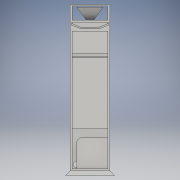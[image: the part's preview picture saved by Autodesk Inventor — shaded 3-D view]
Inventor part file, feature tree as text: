
AUTODESK INVENTOR PART (.ipt)
format: ipt  version: 2016 (Build 200138000, 138)  size: 480,768 bytes
history: native  units: in
note: dims shown in document units (in); Inventor stores cm internally (conversion verified against a paired STEP export)
features: sketch x19, extrude x18, chamfer x1, plane x1, loft x1, shell x1, fillet x1
ambient origin geometry x8: Origin, YZ Plane, XZ Plane, XY Plane, X Axis, Y Axis, Z Axis, Center Point
bodies: Solid1 (feature_tree)
feature tree (42):
  extrude  "Extrusion1"  Depth=18.0in
  extrude  "Extrusion3"  Depth=1.0in
  extrude  "Extrusion4"  Depth=1.0in
  extrude  "Extrusion7"  Depth=2.0in
  extrude  "Extrusion8"  Depth=16.2in
  chamfer  "Chamfer2"  Distance=13.3in
  extrude  "Extrusion9"  Depth=2.0in
  extrude  "Extrusion10"  Depth=2.0in TaperAngle=0.0deg
  sketch  "Sketch12"  dims[d13=2.0in]
  plane  "Work Plane1"
  loft  "Loft1"
  shell  "Shell1"  Thickness=17.0in
  extrude  "Extrusion12"  Depth=2.5in
  extrude  "Extrusion13"  Depth=2.5in
  extrude  "Extrusion14"  Depth=2.5in
  extrude  "Extrusion15"  TaperAngle=0.0deg  [1 undecoded]
  extrude  "Extrusion16"  TaperAngle=0.0deg  [1 undecoded]
  extrude  "Extrusion17"  Depth=2.5in
  extrude  "Extrusion18"  Depth=2.5in TaperAngle=0.0deg
  extrude  "Extrusion19"  Depth=2.5in
  extrude  "Extrusion20"  Depth=2.5in TaperAngle=0.0deg
  extrude  "Extrusion21"  Depth=2.5in
  extrude  "Extrusion22"  Depth=2.5in TaperAngle=0.0deg
  fillet  "Fillet1"  Radius=10.0in
  sketch  "Sketch1"  dims[d0=64.0in d1=18.0in]
  sketch  "Sketch3"  dims[d2=4.0in d3=1.0in]
  sketch  "Sketch4"  dims[d4=1.0in d5=1.0in]
  sketch  "Sketch7"  dims[d6=1.0in d7=2.0in]
  sketch  "Sketch8"  dims[d9=2.0in d10=16.2in]
  sketch  "Sketch9"  dims[d11=8.1in]
  sketch  "Sketch10"  dims[d12=2.56in]
  sketch  "Sketch13"  dims[d14=5.0in]
  sketch  "Sketch14"  dims[d15=5.0in]
  sketch  "Sketch15"  dims[d16=2.0in]
  sketch  "Sketch17"  dims[d17=18.0in]
  sketch  "Sketch18"  dims[d18=0.5in]
  sketch  "Sketch19"  dims[d19=0.5in d20=13.3in d21=0.0in]
  sketch  "Sketch20"  dims[d44=64.0in d45=18.0in d46=4.0in d47=1.0in d48=1.0in d49=1.0in d50=1.0in d51=2.0in d52=2.0in d54=16.2in d55=8.1in d56=2.56in d57=2.0in d58=5.0in d59=5.0in d60=2.0in d61=18.0in d62=0.5in d63=0.5in d64=0.85in d65=0.0in]
  sketch  "Sketch21"  dims[d66=64.0in d67=18.0in d68=4.0in d69=1.0in d70=1.0in d71=1.0in d72=1.0in d73=2.0in d74=2.0in d76=16.2in d77=8.1in d78=2.56in d79=2.0in d80=5.0in d81=5.0in d82=2.0in d83=18.0in d84=0.5in d85=0.5in d86=0.85in d87=0.0in d95=2.0in]
  sketch  "Sketch22"  dims[d96=2.0in d97=0.0in d98=2.0in d99=0.0in]
  sketch  "Sketch23"  dims[d100=2.0in d101=0.125in d102=45.0deg d103=0.5in d105=17.0in d106=0.0in]
  sketch  "Sketch24"  dims[d107=6.5in d108=0.0in d111=2.5in d112=6.5in d113=11.75in d114=0.0in d115=90.0deg d116=0.0in d117=90.0deg d118=0.005in d119=0.5in d120=0.0in d121=0.5in d122=16.0in d123=0.0in d126=18.0in d127=16.0in d128=0.0in d129=10.0in d130=2.5in d131=8.3125in d132=0.0in d133=0.5in d134=4.0in d135=0.5in d136=1.5748in d138=360.0deg d140=2.0in d141=0.0in d144=1.5in d145=1.375in d146=0.0in d147=5.0in d148=2.0in d149=0.5in d150=13.5in d151=0.0in d153=0.5in d154=0.0in d155=3.0in d156=2.0in d157=2.0in d158=21.8125in d159=0.0in d163=14.0in d164=6.75in d165=2.0in d166=14.0in d167=0.0in d171=6.0in d172=0.005in d173=0.0in d174=2.5in d175=16.0in d176=0.5in]
note: 2 required parameter values undecoded (feature->parameter linkage not recoverable at this tier; creation-order binding heuristic only, values carry confidence <= 0.55)
